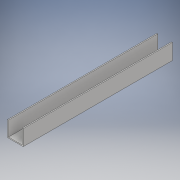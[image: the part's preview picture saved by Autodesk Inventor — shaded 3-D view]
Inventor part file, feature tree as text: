
AUTODESK INVENTOR PART (.ipt)
format: ipt  version: 2017 (Build 210142000, 142)  size: 100,352 bytes
history: native  units: in
note: dims shown in document units (in); Inventor stores cm internally (conversion verified against a paired STEP export)
features: sketch x2, extrude x1
ambient origin geometry x8: Origin, YZ Plane, XZ Plane, XY Plane, X Axis, Y Axis, Z Axis, Center Point
bodies: Solid1 (feature_tree)
feature tree (3):
  sketch  "Sketch1"  dims[d2=0.079in d3=1.26in]
  sketch  "Sketch2"  dims[d5=12.0in d6=0.0in]
  extrude  "Extrusion1"  Depth=1.26in
